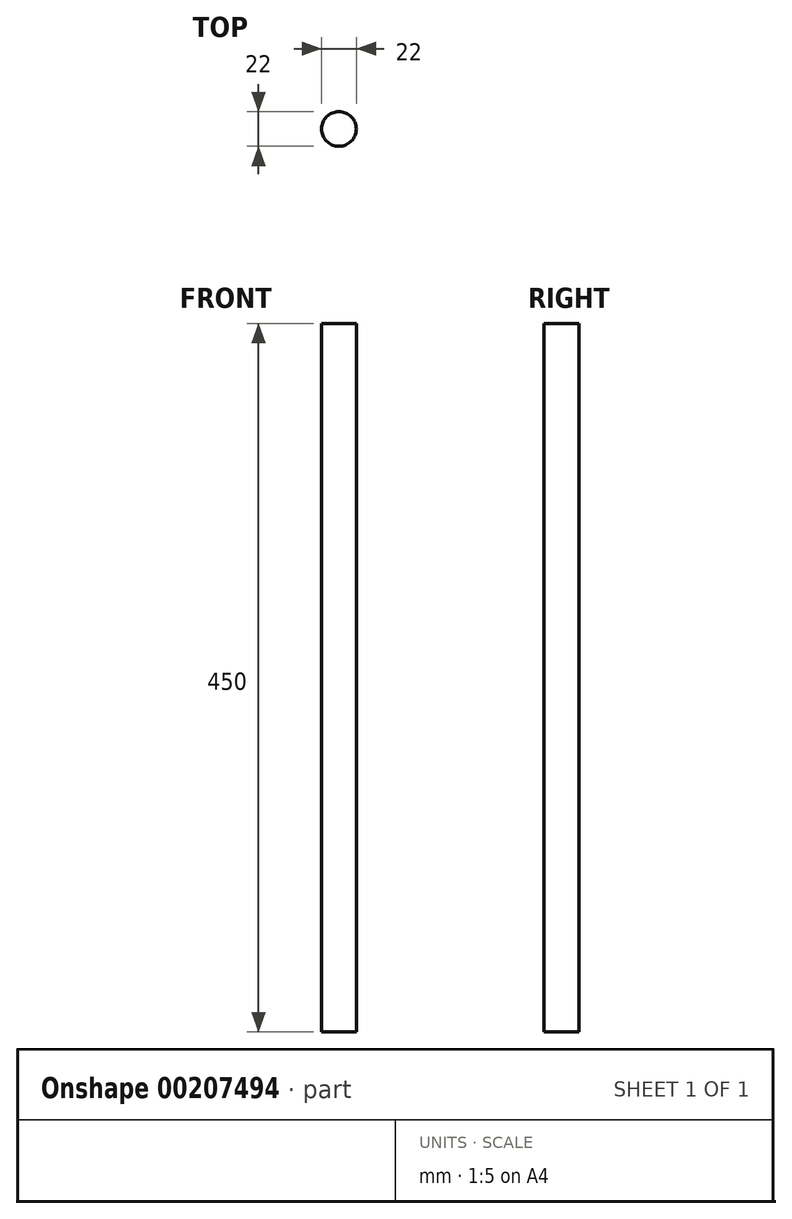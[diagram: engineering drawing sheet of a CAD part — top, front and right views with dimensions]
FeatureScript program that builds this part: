
annotation { "Feature Type Name" : "Feature", "Feature Type Description" : "" }
export const myFeature = defineFeature(function(context is Context, id is Id, definition is map)
    precondition{}
    {
        {
            var Q0;
            Q0=qCreatedBy(makeId("Top.planeOp"),FACE);
            var sketch = newSketch(context, id + "F0", { "sketchPlane" : qUnion([Q0])});
            skCircle(sketch, "E0", {"center": v(0, 0) * mm, "radius": 11 * mm});
            skSolve(sketch);
        }
        {
            var Q0;
            Q0 = qSketchRegion(id + "F0", true);
            extrude(context, id + "F1", {"entities" : qUnion([Q0]), "depth" : 450 * mm});
        }
    });
